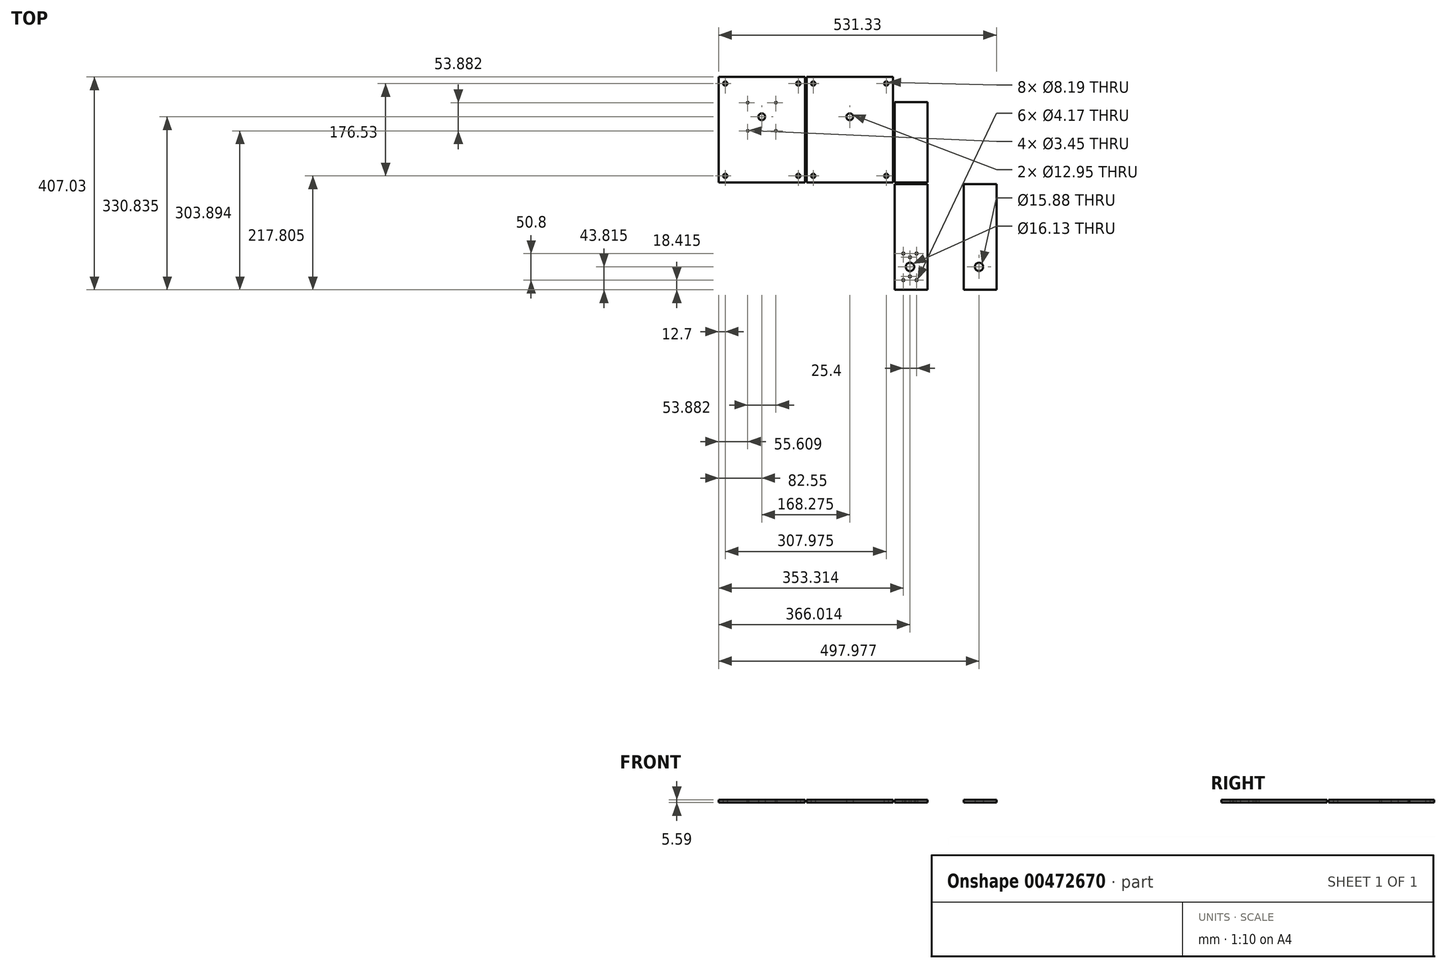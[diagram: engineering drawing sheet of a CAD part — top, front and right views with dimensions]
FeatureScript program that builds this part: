
annotation { "Feature Type Name" : "Feature", "Feature Type Description" : "" }
export const myFeature = defineFeature(function(context is Context, id is Id, definition is map)
    precondition{}
    {
        {
            var Q0;
            Q0=qCreatedBy(makeId("Top.planeOp"),FACE);
            var sketch = newSketch(context, id + "F0", { "sketchPlane" : qUnion([Q0])});
            skLineSegment(sketch, "E0.bottom", {"start": v(0, 0) * mm, "end": v(165.1, 0) * mm});
            skLineSegment(sketch, "E0.top", {"start": v(0, 201.93) * mm, "end": v(165.1, 201.93) * mm});
            skLineSegment(sketch, "E0.left", {"start": v(0, 0) * mm, "end": v(0, 201.93) * mm});
            skLineSegment(sketch, "E0.right", {"start": v(165.1, 0) * mm, "end": v(165.1, 201.93) * mm});
            skLineSegment(sketch, "E1.bottom", {"start": v(168.27, 0) * mm, "end": v(333.38, 0) * mm});
            skLineSegment(sketch, "E1.top", {"start": v(168.27, 201.93) * mm, "end": v(333.38, 201.93) * mm});
            skLineSegment(sketch, "E1.left", {"start": v(168.27, 0) * mm, "end": v(168.27, 201.93) * mm});
            skLineSegment(sketch, "E1.right", {"start": v(333.38, 0) * mm, "end": v(333.37, 201.93) * mm});
            skLineSegment(sketch, "E2.bottom", {"start": v(0, 205.1) * mm, "end": v(165.1, 205.1) * mm});
            skLineSegment(sketch, "E2.top", {"start": v(0, 407.04) * mm, "end": v(165.1, 407.04) * mm});
            skLineSegment(sketch, "E2.left", {"start": v(0, 205.1) * mm, "end": v(0, 407.04) * mm});
            skLineSegment(sketch, "E2.right", {"start": v(165.1, 205.1) * mm, "end": v(165.1, 407.04) * mm});
            skLineSegment(sketch, "E3.bottom", {"start": v(168.27, 205.1) * mm, "end": v(333.37, 205.1) * mm});
            skLineSegment(sketch, "E3.top", {"start": v(168.27, 407.04) * mm, "end": v(333.37, 407.04) * mm});
            skLineSegment(sketch, "E3.left", {"start": v(168.28, 205.1) * mm, "end": v(168.27, 407.04) * mm});
            skLineSegment(sketch, "E3.right", {"start": v(333.37, 205.1) * mm, "end": v(333.37, 407.04) * mm});
            skLineSegment(sketch, "E4", {"start": v(168.27, 205.1) * mm, "end": v(165.1, 205.1) * mm, "construction": true});
            skLineSegment(sketch, "E5", {"start": v(168.27, 205.1) * mm, "end": v(168.27, 201.93) * mm, "construction": true});
            skLineSegment(sketch, "E6.bottom", {"start": v(336.55, 0) * mm, "end": v(399.36, 0) * mm});
            skLineSegment(sketch, "E6.top", {"start": v(336.55, 201.93) * mm, "end": v(399.36, 201.93) * mm});
            skLineSegment(sketch, "E6.left", {"start": v(336.55, 0) * mm, "end": v(336.55, 201.93) * mm});
            skLineSegment(sketch, "E6.right", {"start": v(399.36, 0) * mm, "end": v(399.36, 201.93) * mm});
            skLineSegment(sketch, "E7.bottom", {"start": v(336.55, 205.1) * mm, "end": v(399.36, 205.1) * mm});
            skLineSegment(sketch, "E7.top", {"start": v(336.55, 359.03) * mm, "end": v(399.36, 359.03) * mm});
            skLineSegment(sketch, "E7.left", {"start": v(336.55, 205.1) * mm, "end": v(336.55, 359.03) * mm});
            skLineSegment(sketch, "E7.right", {"start": v(399.36, 205.1) * mm, "end": v(399.36, 359.03) * mm});
            skLineSegment(sketch, "E8.1.0.0", {"start": v(402.53, 359.03) * mm, "end": v(465.34, 359.03) * mm});
            skLineSegment(sketch, "E8.1.0.1", {"start": v(465.34, 205.1) * mm, "end": v(465.34, 359.03) * mm});
            skLineSegment(sketch, "E8.1.0.2", {"start": v(402.53, 205.1) * mm, "end": v(402.53, 359.03) * mm});
            skLineSegment(sketch, "E8.1.0.3", {"start": v(402.53, 205.1) * mm, "end": v(465.34, 205.1) * mm});
            skLineSegment(sketch, "E8.1.0.4", {"start": v(402.53, 201.93) * mm, "end": v(465.34, 201.93) * mm});
            skLineSegment(sketch, "E8.1.0.5", {"start": v(402.53, 0) * mm, "end": v(402.53, 201.93) * mm});
            skLineSegment(sketch, "E8.1.0.6", {"start": v(465.34, 0) * mm, "end": v(465.34, 201.93) * mm});
            skLineSegment(sketch, "E8.1.0.7", {"start": v(402.53, 0) * mm, "end": v(465.34, 0) * mm});
            skLineSegment(sketch, "E8.2.0.0", {"start": v(468.52, 359.03) * mm, "end": v(531.33, 359.03) * mm});
            skLineSegment(sketch, "E8.2.0.1", {"start": v(531.33, 205.1) * mm, "end": v(531.33, 359.03) * mm});
            skLineSegment(sketch, "E8.2.0.2", {"start": v(468.52, 205.1) * mm, "end": v(468.52, 359.03) * mm});
            skLineSegment(sketch, "E8.2.0.3", {"start": v(468.52, 205.1) * mm, "end": v(531.33, 205.1) * mm});
            skLineSegment(sketch, "E8.2.0.4", {"start": v(468.52, 201.93) * mm, "end": v(531.33, 201.93) * mm});
            skLineSegment(sketch, "E8.2.0.5", {"start": v(468.52, 0) * mm, "end": v(468.52, 201.93) * mm});
            skLineSegment(sketch, "E8.2.0.6", {"start": v(531.33, 0) * mm, "end": v(531.33, 201.93) * mm});
            skLineSegment(sketch, "E8.2.0.7", {"start": v(468.52, 0) * mm, "end": v(531.33, 0) * mm});
            skLineSegment(sketch, "E8.3.0.0", {"start": v(534.5, 359.03) * mm, "end": v(597.31, 359.03) * mm});
            skLineSegment(sketch, "E8.3.0.1", {"start": v(597.31, 205.1) * mm, "end": v(597.31, 359.03) * mm});
            skLineSegment(sketch, "E8.3.0.2", {"start": v(534.5, 205.1) * mm, "end": v(534.5, 359.03) * mm});
            skLineSegment(sketch, "E8.3.0.3", {"start": v(534.5, 205.1) * mm, "end": v(597.31, 205.1) * mm});
            skLineSegment(sketch, "E8.3.0.4", {"start": v(534.5, 201.93) * mm, "end": v(597.31, 201.93) * mm});
            skLineSegment(sketch, "E8.3.0.5", {"start": v(534.5, 0) * mm, "end": v(534.5, 201.93) * mm});
            skLineSegment(sketch, "E8.3.0.6", {"start": v(597.31, 0) * mm, "end": v(597.31, 201.93) * mm});
            skLineSegment(sketch, "E8.3.0.7", {"start": v(534.5, 0) * mm, "end": v(597.31, 0) * mm});
            skLineSegment(sketch, "E8.direction1", {"start": v(336.55, 0) * mm, "end": v(402.53, 0) * mm, "construction": true});
            skCircle(sketch, "E9", {"center": v(12.7, 394.34) * mm, "radius": 4.1 * mm});
            skCircle(sketch, "E10", {"center": v(82.55, 330.84) * mm, "radius": 6.48 * mm});
            skCircle(sketch, "E11", {"center": v(366.01, 43.82) * mm, "radius": 8.06 * mm});
            skCircle(sketch, "E12.0.1.0", {"center": v(12.7, 217.8) * mm, "radius": 4.1 * mm});
            skCircle(sketch, "E12.1.0.0", {"center": v(152.4, 394.34) * mm, "radius": 4.1 * mm});
            skCircle(sketch, "E12.1.1.0", {"center": v(152.4, 217.8) * mm, "radius": 4.1 * mm});
            skLineSegment(sketch, "E12.direction1", {"start": v(12.7, 394.34) * mm, "end": v(152.4, 394.34) * mm, "construction": true});
            skLineSegment(sketch, "E12.direction2", {"start": v(12.7, 394.34) * mm, "end": v(12.7, 217.8) * mm, "construction": true});
            skLineSegment(sketch, "E13", {"start": v(82.55, 330.84) * mm, "end": v(82.55, 407.04) * mm, "construction": true});
            skCircle(sketch, "E14.1.0.0", {"center": v(320.67, 394.34) * mm, "radius": 4.1 * mm});
            skCircle(sketch, "E14.1.0.1", {"center": v(250.83, 330.84) * mm, "radius": 6.48 * mm});
            skCircle(sketch, "E14.1.0.2", {"center": v(320.68, 217.8) * mm, "radius": 4.1 * mm});
            skLineSegment(sketch, "E14.1.0.3", {"start": v(180.97, 394.34) * mm, "end": v(320.67, 394.34) * mm});
            skCircle(sketch, "E14.1.0.4", {"center": v(180.97, 217.8) * mm, "radius": 4.1 * mm});
            skLineSegment(sketch, "E14.1.0.5", {"start": v(180.97, 394.34) * mm, "end": v(180.97, 217.8) * mm, "construction": true});
            skCircle(sketch, "E14.1.0.6", {"center": v(180.97, 394.34) * mm, "radius": 4.1 * mm});
            skLineSegment(sketch, "E14.direction1", {"start": v(12.7, 217.8) * mm, "end": v(180.97, 217.8) * mm, "construction": true});
            skLineSegment(sketch, "E15", {"start": v(366.01, 43.82) * mm, "end": v(366.01, 0) * mm, "construction": true});
            skCircle(sketch, "E16", {"center": v(432, 43.82) * mm, "radius": 8.06 * mm});
            skLineSegment(sketch, "E17", {"start": v(432, 43.82) * mm, "end": v(432, 0) * mm, "construction": true});
            skCircle(sketch, "E18.0.1.0", {"center": v(12.7, 189.23) * mm, "radius": 4.1 * mm});
            skCircle(sketch, "E18.0.1.1", {"center": v(152.4, 189.23) * mm, "radius": 4.1 * mm});
            skCircle(sketch, "E18.0.1.2", {"center": v(152.4, 12.7) * mm, "radius": 4.1 * mm});
            skCircle(sketch, "E18.0.1.3", {"center": v(12.7, 12.7) * mm, "radius": 4.1 * mm});
            skCircle(sketch, "E18.0.1.4", {"center": v(82.55, 125.73) * mm, "radius": 6.48 * mm});
            skCircle(sketch, "E18.0.1.5", {"center": v(250.83, 125.73) * mm, "radius": 6.48 * mm});
            skCircle(sketch, "E18.0.1.6", {"center": v(180.97, 189.23) * mm, "radius": 4.1 * mm});
            skCircle(sketch, "E18.0.1.7", {"center": v(320.67, 189.23) * mm, "radius": 4.1 * mm});
            skCircle(sketch, "E18.0.1.8", {"center": v(320.68, 12.7) * mm, "radius": 4.1 * mm});
            skCircle(sketch, "E18.0.1.9", {"center": v(180.97, 12.7) * mm, "radius": 4.1 * mm});
            skLineSegment(sketch, "E18.direction1", {"start": v(12.7, 394.34) * mm, "end": v(518.16, 394.34) * mm, "construction": true});
            skLineSegment(sketch, "E18.direction2", {"start": v(12.7, 394.34) * mm, "end": v(12.7, 189.23) * mm, "construction": true});
            skLineSegment(sketch, "E19", {"start": v(497.98, 43.82) * mm, "end": v(497.98, 0) * mm, "construction": true});
            skLineSegment(sketch, "E20", {"start": v(563.96, 43.82) * mm, "end": v(563.96, 0) * mm, "construction": true});
            skCircle(sketch, "E21", {"center": v(366.01, 62.07) * mm, "radius": 2.08 * mm});
            skLineSegment(sketch, "E22", {"start": v(366.01, 43.82) * mm, "end": v(366.01, 62.07) * mm, "construction": true});
            skLineSegment(sketch, "E23", {"start": v(366.01, 43.82) * mm, "end": v(395.7, 43.82) * mm, "construction": true});
            skCircle(sketch, "E24.MirrorC", {"center": v(366.01, 25.56) * mm, "radius": 2.08 * mm});
            skCircle(sketch, "E25", {"center": v(497.98, 43.82) * mm, "radius": 7.94 * mm});
            skCircle(sketch, "E26", {"center": v(563.96, 43.82) * mm, "radius": 7.94 * mm});
            skLineSegment(sketch, "E27.bottom", {"start": v(353.31, 69.22) * mm, "end": v(378.71, 69.22) * mm, "construction": true});
            skLineSegment(sketch, "E27.top", {"start": v(353.31, 18.41) * mm, "end": v(378.71, 18.41) * mm, "construction": true});
            skLineSegment(sketch, "E27.left", {"start": v(353.31, 69.22) * mm, "end": v(353.31, 18.42) * mm, "construction": true});
            skLineSegment(sketch, "E27.right", {"start": v(378.71, 69.22) * mm, "end": v(378.71, 18.41) * mm, "construction": true});
            skCircle(sketch, "E28", {"center": v(353.31, 69.22) * mm, "radius": 2.08 * mm});
            skCircle(sketch, "E29", {"center": v(378.71, 69.22) * mm, "radius": 2.08 * mm});
            skCircle(sketch, "E30", {"center": v(378.71, 18.41) * mm, "radius": 2.08 * mm});
            skCircle(sketch, "E31", {"center": v(353.31, 18.41) * mm, "radius": 2.08 * mm});
            skCircle(sketch, "E32", {"center": v(109.5, 357.78) * mm, "radius": 1.73 * mm});
            skLineSegment(sketch, "E33", {"start": v(82.55, 330.83) * mm, "end": v(109.5, 357.78) * mm, "construction": true});
            skCircle(sketch, "E34.1.0", {"center": v(55.6, 357.78) * mm, "radius": 1.73 * mm});
            skCircle(sketch, "E34.2.0", {"center": v(55.6, 303.9) * mm, "radius": 1.73 * mm});
            skCircle(sketch, "E34.3.0", {"center": v(109.5, 303.9) * mm, "radius": 1.73 * mm});
            skSolve(sketch);
        }
        {
            var Q0;
            Q0=makeQuery(id+"F0.imprint","IMPRINT",FACE,{"disambiguationData":[TD([[makeQuery(id+"F0.imprint","IMPRINT",EDGE,{"derivedFrom":sQuery(id+"F0.wireOp",EDGE,"E2.bottom")}),1.0]])]});
            extrude(context, id + "F1", {"entities" : qUnion([Q0]), "depth" : 5.6 * mm});
        }
        {
            var Q0;
            Q0=makeQuery(id+"F0.imprint","IMPRINT",FACE,{"disambiguationData":[TD([[makeQuery(id+"F0.imprint","IMPRINT",EDGE,{"derivedFrom":sQuery(id+"F0.wireOp",EDGE,"E6.bottom")}),1.0]])]});
            extrude(context, id + "F2", {"entities" : qUnion([Q0]), "depth" : 5.6 * mm});
        }
        {
            var Q0;
            Q0=makeQuery(id+"F0.imprint","IMPRINT",FACE,{"disambiguationData":[TD([[makeQuery(id+"F0.imprint","IMPRINT",EDGE,{"derivedFrom":sQuery(id+"F0.wireOp",EDGE,"E7.bottom")}),1.0]])]});
            extrude(context, id + "F3", {"entities" : qUnion([Q0]), "depth" : 5.6 * mm});
        }
        {
            var Q0;
            Q0=makeQuery(id+"F0.imprint","IMPRINT",FACE,{"disambiguationData":[TD([[makeQuery(id+"F0.imprint","IMPRINT",EDGE,{"derivedFrom":sQuery(id+"F0.wireOp",EDGE,"E8.2.0.4")}),-1.0]])]});
            extrude(context, id + "F4", {"entities" : qUnion([Q0]), "depth" : 5.6 * mm});
        }
        {
            var Q0;
            Q0=makeQuery(id+"F0.imprint","IMPRINT",FACE,{"disambiguationData":[TD([[makeQuery(id+"F0.imprint","IMPRINT",EDGE,{"derivedFrom":sQuery(id+"F0.wireOp",EDGE,"E3.bottom")}),1.0]])]});
            extrude(context, id + "F5", {"entities" : qUnion([Q0]), "depth" : 5.6 * mm});
        }
    });
